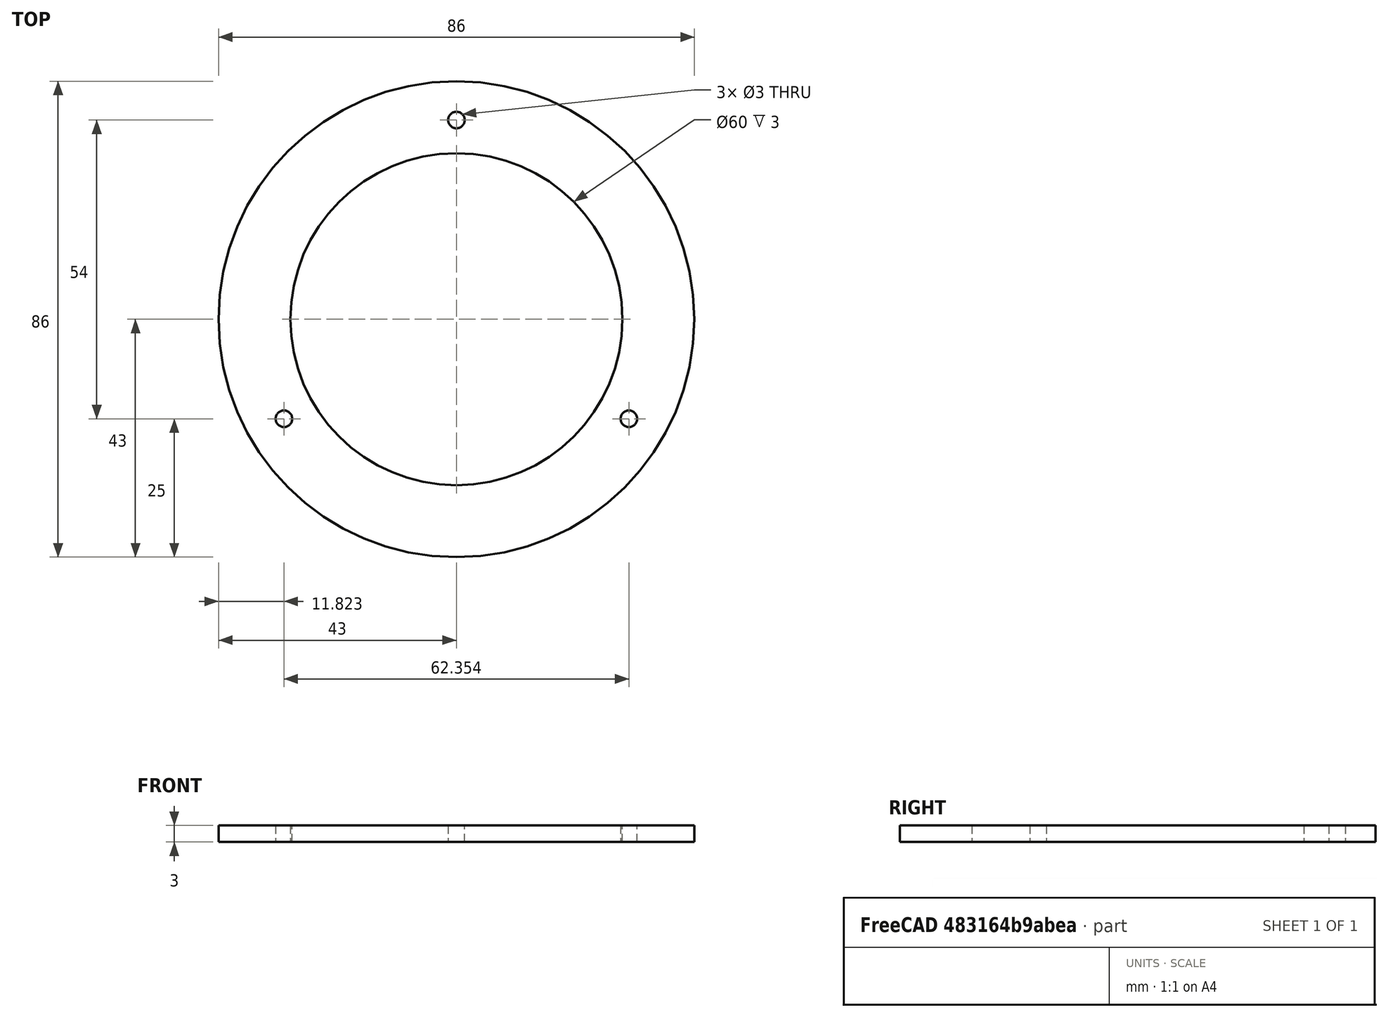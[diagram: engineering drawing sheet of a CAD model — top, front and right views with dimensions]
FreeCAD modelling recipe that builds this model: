
FCSTD DOCUMENT  (FreeCAD 0.19R24276 (Git))
Label: Ring_underglass_h_3_0mm_V5
License: All rights reserved
LicenseURL: http://en.wikipedia.org/wiki/All_rights_reserved
objects: Sketcher::SketchObject×1, PartDesign::Pad×1, PartDesign::Body×1
note: 4 computed .brp shape members not serialized (recipe doc carries the construction recipe); baked Part::Feature solids carry a one-line shape summary decoded from their .brp

FEATURE [Sketcher::SketchObject] Sketch006  label="Sketch006_d72_3_otv_d3"
  FullyConstrained = true
  MapMode = 5
  Placement = pos=(0,0,22) rot=(0,0,1;0rad)
  sketch-geometry (9):
    g0: LineSegment StartX=0 StartY=36 StartZ=0 EndX=-31.1769 EndY=-18 EndZ=0
    g1: LineSegment StartX=-31.1769 StartY=-18 StartZ=0 EndX=31.1769 EndY=-18 EndZ=0
    g2: LineSegment StartX=31.1769 StartY=-18 StartZ=0 EndX=0 EndY=36 EndZ=0
    g3: Circle CenterX=0 CenterY=0 CenterZ=0 NormalX=0 NormalY=0 NormalZ=1 AngleXU=0 Radius=36
    g4: Circle CenterX=0 CenterY=36 CenterZ=0 NormalX=0 NormalY=0 NormalZ=1 AngleXU=0 Radius=1.5
    g5: Circle CenterX=31.1769 CenterY=-18 CenterZ=0 NormalX=0 NormalY=0 NormalZ=1 AngleXU=0 Radius=1.5
    g6: Circle CenterX=-31.1769 CenterY=-18 CenterZ=0 NormalX=0 NormalY=0 NormalZ=1 AngleXU=0 Radius=1.5
    g7: Circle CenterX=0 CenterY=0 CenterZ=0 NormalX=0 NormalY=0 NormalZ=1 AngleXU=0 Radius=43
    g8: Circle CenterX=0 CenterY=0 CenterZ=0 NormalX=0 NormalY=0 NormalZ=1 AngleXU=0 Radius=30
  constraints (21):
    c: Coincident(g0,g1)
    c: Coincident(g1,g2)
    c: Coincident(g2,g0)
    c: Equal(g0,g1)
    c: Equal(g0,g2)
    c: PointOnObject(g0,g3)
    c: PointOnObject(g1,g3)
    c: PointOnObject(g2,g3)
    c: Coincident(g3,g-1)
    c: PointOnObject(g2,g-2)
    c: Diameter(g3) = 72
    c: Coincident(g4,g0)
    c: Coincident(g5,g1)
    c: Coincident(g6,g0)
    c: Diameter(g6) = 3
    c: Equal(g6,g4)
    c: Equal(g6,g5)
    c: Coincident(g7,g-1)
    c: Diameter(g7) = 86
    c: Coincident(g8,g7)
    c: Diameter(g8) = 60
FEATURE [PartDesign::Pad] Pad  label="Pad_h3"
  Direction = (1,1,1)
  Length = 3
  Length2 = 100
  Placement = pos=(0,0,22) rot=(0,0,1;0rad)
  Profile = -> Sketch006
  Type = 0
FEATURE [PartDesign::Body] Body
  Group = -> [Sketch006,Pad]
  Origin = -> Origin
  Tip = -> Pad
